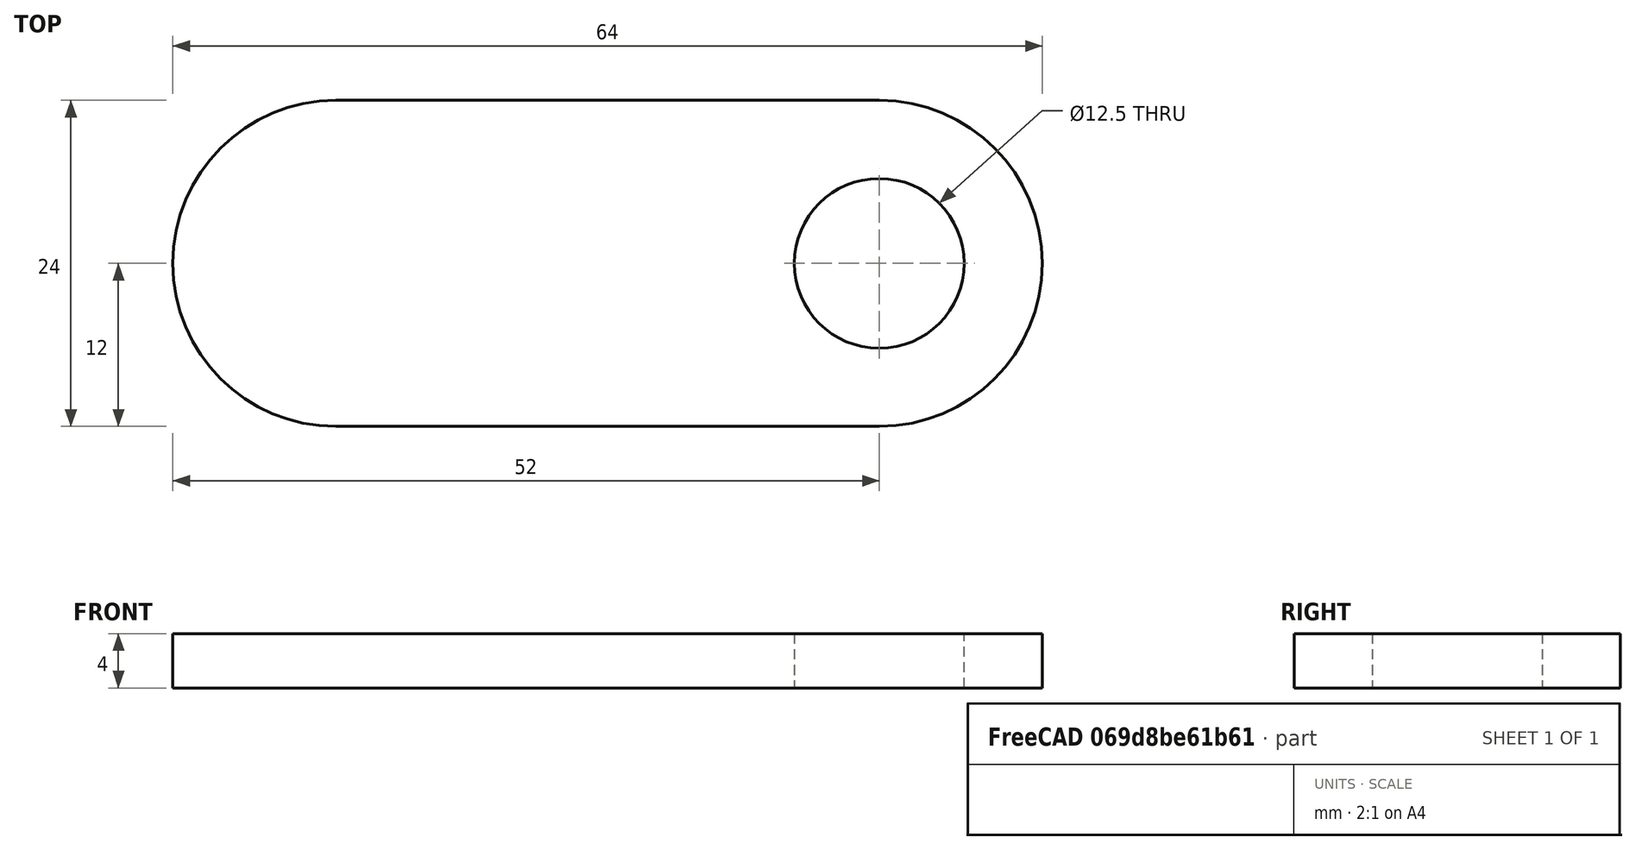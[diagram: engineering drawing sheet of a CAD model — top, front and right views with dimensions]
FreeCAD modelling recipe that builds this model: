
FCSTD DOCUMENT  (FreeCAD 0.19R24267 +99 (Git))
Label: V2 Actuator pin retainer plate
License: All rights reserved
LicenseURL: http://en.wikipedia.org/wiki/All_rights_reserved
objects: Sketcher::SketchObject×1, PartDesign::Pad×1, PartDesign::Body×1
note: 4 computed .brp shape members not serialized (recipe doc carries the construction recipe); baked Part::Feature solids carry a one-line shape summary decoded from their .brp

FEATURE [Sketcher::SketchObject] Sketch
  FullyConstrained = true
  MapMode = 5
  Support = -> [XY_Plane]
  sketch-geometry (5):
    g0: ArcOfCircle CenterX=0 CenterY=0 CenterZ=0 NormalX=0 NormalY=0 NormalZ=1 AngleXU=0 Radius=12 StartAngle=4.71239 EndAngle=7.85398
    g1: ArcOfCircle CenterX=-40 CenterY=0 CenterZ=0 NormalX=0 NormalY=0 NormalZ=1 AngleXU=0 Radius=12 StartAngle=1.5708 EndAngle=4.71239
    g2: LineSegment StartX=-40 StartY=12 StartZ=0 EndX=7.1e-15 EndY=12 EndZ=0
    g3: LineSegment StartX=-40 StartY=-12 StartZ=0 EndX=0 EndY=-12 EndZ=0
    g4: Circle CenterX=0 CenterY=0 CenterZ=0 NormalX=0 NormalY=0 NormalZ=1 AngleXU=0 Radius=6.25
  constraints (13):
    c: Coincident(g0,g-1)
    c: PointOnObject(g1,g-1)
    c: Equal(g0,g1)
    c: Radius(g1) = 12
    c: DistanceX(g1,g0) = 40
    c: Horizontal(g2)
    c: Horizontal(g3)
    c: Coincident(g1,g2)
    c: Coincident(g1,g3)
    c: Tangent(g0,g2) = 1.5708
    c: Tangent(g0,g3) = -1.5708
    c: Coincident(g4,g0)
    c: Diameter(g4) = 12.5
FEATURE [PartDesign::Pad] Pad
  Direction = (1,1,1)
  Length = 4
  Length2 = 100
  Profile = -> Sketch
  Type = 0
FEATURE [PartDesign::Body] Body
  Group = -> [Sketch,Pad]
  Origin = -> Origin
  Tip = -> Pad
